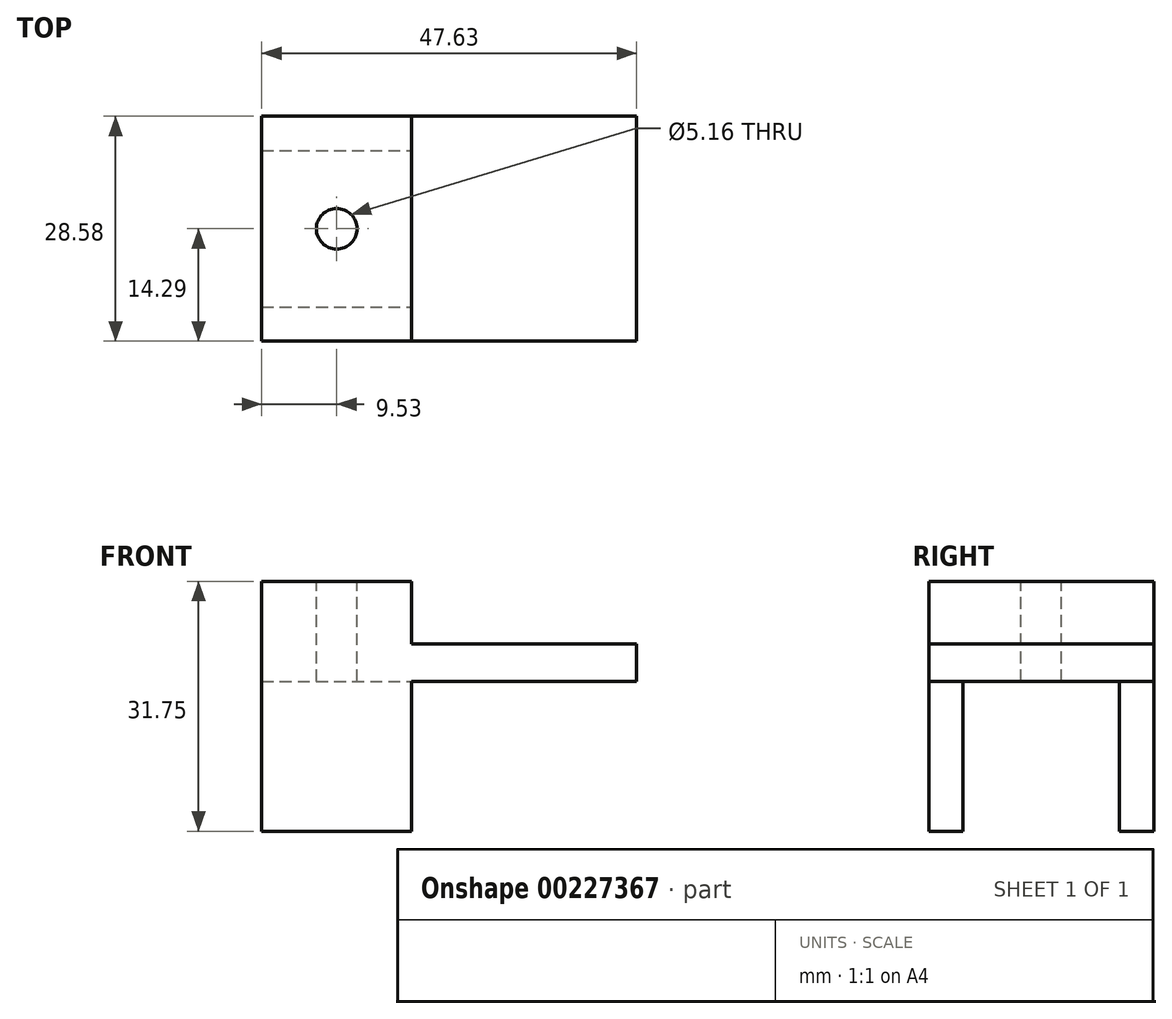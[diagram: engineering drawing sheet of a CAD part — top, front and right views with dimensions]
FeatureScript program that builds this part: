
annotation { "Feature Type Name" : "Feature", "Feature Type Description" : "" }
export const myFeature = defineFeature(function(context is Context, id is Id, definition is map)
    precondition{}
    {
        {
            var Q0;
            Q0=qCreatedBy(makeId("Top.planeOp"),FACE);
            var sketch = newSketch(context, id + "F0", { "sketchPlane" : qUnion([Q0])});
            skLineSegment(sketch, "E0.bottom", {"start": v(9.53, 14.29) * mm, "end": v(-9.53, 14.29) * mm});
            skLineSegment(sketch, "E0.top", {"start": v(9.52, -14.29) * mm, "end": v(-9.53, -14.29) * mm});
            skLineSegment(sketch, "E0.left", {"start": v(9.53, 14.29) * mm, "end": v(9.52, -14.29) * mm});
            skLineSegment(sketch, "E0.right", {"start": v(-9.53, 14.29) * mm, "end": v(-9.53, -14.29) * mm});
            skPoint(sketch, "E0.middle", {"position": v(0, 0) * mm});
            skSolve(sketch);
        }
        {
            var Q0;
            Q0=makeQuery(id+"F0.imprint","IMPRINT",FACE,{"disambiguationData":[TD([[makeQuery(id+"F0.imprint","IMPRINT",EDGE,{"derivedFrom":sQuery(id+"F0.wireOp",EDGE,"E0.bottom")}),1.0]])]});
            extrude(context, id + "F1", {"entities" : qUnion([Q0]), "depth" : 31.75 * mm});
        }
        {
            var Q0;
            Q0=makeQuery(id+"F1.opExtrude","SWEPT_FACE",FACE,{"disambiguationData":[OSD([sQuery(id+"F0.wireOp",EDGE,"E0.left")])]});
            var sketch = newSketch(context, id + "F2", { "sketchPlane" : qUnion([Q0])});
            skLineSegment(sketch, "E1.bottom", {"start": v(-9.92, 0) * mm, "end": v(9.92, 0) * mm});
            skLineSegment(sketch, "E1.top", {"start": v(-9.92, 19.05) * mm, "end": v(9.92, 19.05) * mm});
            skLineSegment(sketch, "E1.left", {"start": v(-9.92, 0) * mm, "end": v(-9.92, 19.05) * mm});
            skLineSegment(sketch, "E1.right", {"start": v(9.92, 0) * mm, "end": v(9.92, 19.05) * mm});
            skSolve(sketch);
        }
        {
            var Q0;
            Q0=makeQuery(id+"F2.imprint","IMPRINT",FACE,{"disambiguationData":[TD([[makeQuery(id+"F2.imprint","IMPRINT",EDGE,{"derivedFrom":sQuery(id+"F2.wireOp",EDGE,"E1.bottom")}),-1.0]])]});
            extrude(context, id + "F3", {"entities" : qUnion([Q0]), "operationType" : NewBodyOperationType.REMOVE, "endBound" : BoundingType.THROUGH_ALL, "oppositeDirection" : true, "depth" : 25.4 * mm});
        }
        {
            var Q0;
            Q0=qCreatedBy(makeId("Right.planeOp"),FACE);
            var sketch = newSketch(context, id + "F4", { "sketchPlane" : qUnion([Q0])});
            skLineSegment(sketch, "E2.bottom", {"start": v(-14.29, 19.05) * mm, "end": v(14.29, 19.05) * mm});
            skLineSegment(sketch, "E2.top", {"start": v(-14.29, 23.81) * mm, "end": v(14.29, 23.81) * mm});
            skLineSegment(sketch, "E2.left", {"start": v(-14.29, 19.05) * mm, "end": v(-14.29, 23.81) * mm});
            skLineSegment(sketch, "E2.right", {"start": v(14.29, 19.05) * mm, "end": v(14.29, 23.81) * mm});
            skSolve(sketch);
        }
        {
            var Q0;
            Q0 = qSketchRegion(id + "F4", true);
            extrude(context, id + "F5", {"entities" : qUnion([Q0]), "operationType" : NewBodyOperationType.ADD, "depth" : 38.1 * mm});
        }
        {
            var Q0;
            Q0=makeQuery(id+"F1.opExtrude","CAP_FACE",FACE,{"disambiguationData":[OSD([sQuery(id+"F0.wireOp",EDGE,"E0.bottom"),sQuery(id+"F0.wireOp",EDGE,"E0.top"),sQuery(id+"F0.wireOp",EDGE,"E0.left"),sQuery(id+"F0.wireOp",EDGE,"E0.right")])],"isStart":false});
            var sketch = newSketch(context, id + "F6", { "sketchPlane" : qUnion([Q0])});
            skCircle(sketch, "E3", {"center": v(0, 0) * mm, "radius": 2.58 * mm});
            skSolve(sketch);
        }
        {
            var Q0;
            Q0=makeQuery(id+"F6.imprint","IMPRINT",FACE,{"disambiguationData":[TD([[makeQuery(id+"F6.imprint","IMPRINT",EDGE,{"derivedFrom":sQuery(id+"F6.wireOp",EDGE,"E3")}),1.0]])]});
            extrude(context, id + "F7", {"entities" : qUnion([Q0]), "operationType" : NewBodyOperationType.REMOVE, "endBound" : BoundingType.THROUGH_ALL, "oppositeDirection" : true, "depth" : 25.4 * mm});
        }
    });
